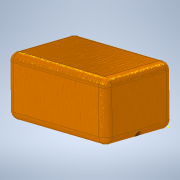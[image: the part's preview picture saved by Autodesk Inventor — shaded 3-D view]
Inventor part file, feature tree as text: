
AUTODESK INVENTOR PART (.ipt)
format: ipt  version: 2021.3 (Build 253353000, 353)  size: 181,248 bytes
history: native  units: in
note: dims shown in document units (in); Inventor stores cm internally (conversion verified against a paired STEP export)
features: other x3, sketch x2, extrude x1, fillet x1
ambient origin geometry x8: Origin, YZ Plane, XZ Plane, XY Plane, X Axis, Y Axis, Z Axis, Center Point
bodies: Solid1 (feature_tree)
feature tree (7):
  other  "Box 1.ipt"
  sketch  "Sketch1"  dims[d0=0.3937in d1=0.0in d2=0.0in d3=0.3937in]
  extrude  "Extrusion1"  TaperAngle=0.0deg  [1 undecoded]
  fillet  "Fillet1"  Radius=0.3937in
  other  "Solid1::Box 1.ipt"
  other  "TaggingFeature1"
  sketch  "Sketch2"
note: 1 required parameter value undecoded (feature->parameter linkage not recoverable at this tier; creation-order binding heuristic only, values carry confidence <= 0.55)
